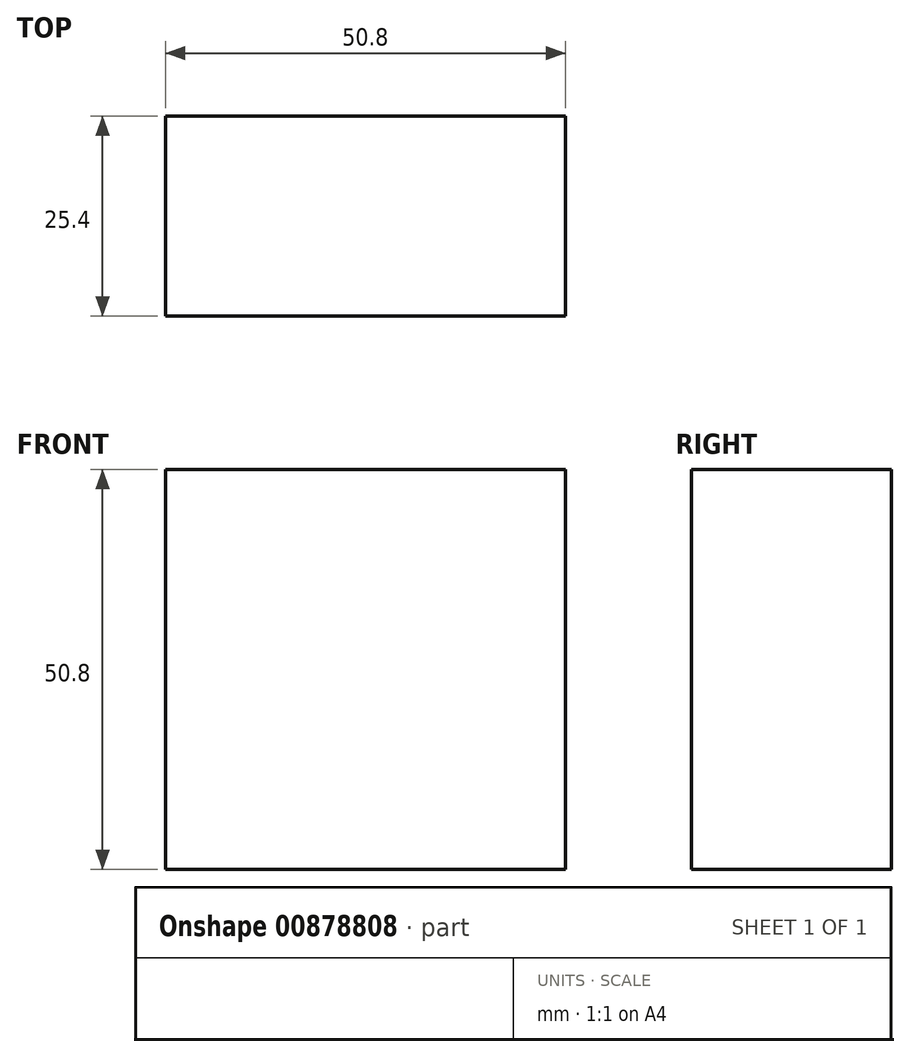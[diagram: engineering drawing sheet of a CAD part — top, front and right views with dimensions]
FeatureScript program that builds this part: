
annotation { "Feature Type Name" : "Feature", "Feature Type Description" : "" }
export const myFeature = defineFeature(function(context is Context, id is Id, definition is map)
    precondition{}
    {
        {
            var Q0;
            Q0=qCreatedBy(makeId("Front.planeOp"),FACE);
            var sketch = newSketch(context, id + "F0", { "sketchPlane" : qUnion([Q0])});
            skLineSegment(sketch, "E0.bottom", {"start": v(-25.4, 25.4) * mm, "end": v(25.4, 25.4) * mm});
            skLineSegment(sketch, "E0.top", {"start": v(-25.4, -25.4) * mm, "end": v(25.4, -25.4) * mm});
            skLineSegment(sketch, "E0.left", {"start": v(-25.4, 25.4) * mm, "end": v(-25.4, -25.4) * mm});
            skLineSegment(sketch, "E0.right", {"start": v(25.4, 25.4) * mm, "end": v(25.4, -25.4) * mm});
            skLineSegment(sketch, "E1", {"start": v(0, 25.4) * mm, "end": v(0, -41.3) * mm, "construction": true});
            skSolve(sketch);
        }
        {
            var Q0;
            Q0 = qSketchRegion(id + "F0", true);
            extrude(context, id + "F1", {"entities" : qUnion([Q0]), "endBound" : BoundingType.SYMMETRIC, "depth" : 25.4 * mm, "offsetDistance" : 25.4 * mm});
        }
    });
